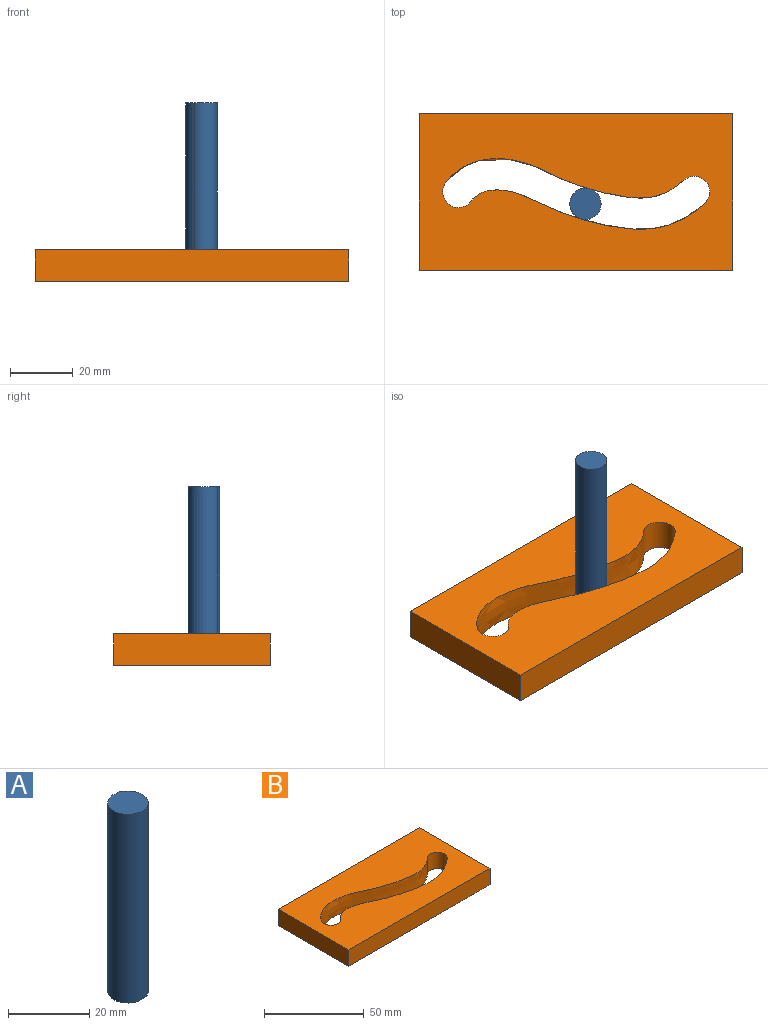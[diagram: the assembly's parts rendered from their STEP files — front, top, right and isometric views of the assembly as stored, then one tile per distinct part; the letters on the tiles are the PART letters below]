
ASSEMBLY  parts=2 mates=1
PART A: 4 faces, bbox 10x10x57 mm
  f0: cylinder r=5mm len=57mm, axis (0,0,-1), area 895.4mm2, adj f1,f2,f3
  f1: extruded ~57x9mm, area 895.5mm2, adj f0,f2,f3
  f2: plane 10x10mm, normal (0,0,1), area 78.5mm2, adj f0,f1
  f3: plane 10x10mm, normal (0,0,-1), area 78.5mm2, adj f0,f1
PART B: 10 faces, bbox 100x50x10 mm
  f0: plane 100x10mm, normal (0,1,0), area 1000mm2, adj f1,f3,f4,f5
  f1: plane 50x10mm, normal (-1,0,0), area 500mm2, adj f0,f2,f4,f5
  f2: plane 100x10mm, normal (0,-1,0), area 1000mm2, adj f1,f3,f4,f5
  f3: plane 50x10mm, normal (1,0,0), area 500mm2, adj f0,f2,f4,f5
  f4: plane 100x50mm, normal (0,0,1), area 4111.9mm2, adj f0,f1,f2,f3,f6,f7,f8,f9
  f5: plane 100x50mm, normal (0,0,-1), area 4111.9mm2, adj f0,f1,f2,f3,f6,f7,f8,f9
  f6: extruded ~76.04x12.58mm, area 820.6mm2, adj f4,f5,f7,f9
  f7: cylinder r=5mm len=10mm, axis (0,0,1), area 157.1mm2, adj f4,f5,f6,f8
  f8: extruded ~74.59x12.59mm, area 799.4mm2, adj f4,f5,f7,f9
  f9: cylinder r=5mm len=10mm, axis (0,0,1), area 157.1mm2, adj f4,f5,f6,f8
PLACE A rot(axis=(0,0,1),98.9deg) t=(-24.85,42.1,3.87)mm
PLACE B t=(-22.06,8.84,3.87)mm fixed
MATE planar A.f0 <-> B.f5  axis (0,0,-1) through (-19.05,4.99,3.87)mm
